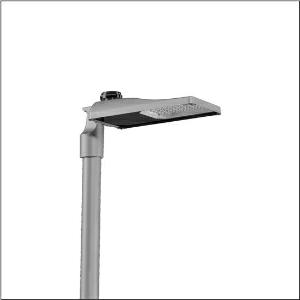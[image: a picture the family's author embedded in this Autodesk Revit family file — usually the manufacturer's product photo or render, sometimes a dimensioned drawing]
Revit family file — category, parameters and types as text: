
# Revit family: streetlight_sl_31_mini___st1_0a_5xh6d35n08ha_c5a6
name_source: partatom
category: Lighting Fixtures
units: mm (PartAtom-declared; Revit-internal decimal feet)

## family parameters
Cut with Voids When Loaded = No
Host = Face
Light Source = No
Part Type = Normal
Room Calculation Point = No
Round Connector Dimension = Use Diameter
Shared = No

## types (1)
- --- (1 x LED, 9240 lm, 68.3 W, 3000K)
    Apparent Load = 68 VA
    CIE Flux Codes = 37 72 97 100 100
    Color Rendering = 70
    Color Temperature = 3000K
    Default Elevation = 1800 mm
    Description = Streetlight SL 31 mini, mast luminaire, primary light control with lens, of PMMA, primary optical cover: cover, of toughened safety glass, transparent, light distribution: ST1.0a, light emission: direct distribution, primary light characteristic: asymmetric, installation type: post-top, side-entry, LED, High Power LED, rated luminous flux: 9.240lm, luminous efficacy: 135lm/W, light colour: 730, colour temperature: 3000K, control: presetting dimming linear, flexible luminous flux parameterisation, time-dependent luminous flux control, constant luminous flux control, intelligent temperature release in ECG and LED module, overheat protection, with cable H07RN-F 3x 1.5mm², mains connection: 220..240V, AC, 50/60Hz, connection cable pre-assembled, cable length: 8,5m, start of lifetime: 68W, end of service life: 75W, reduction: 30W, luminaire housing, of diecast aluminium, powder-coated, Siteco® metallic grey (DB 702S), corrosivity category C5 high according to DIN EN ISO 12944, no sealing on luminaire upper side, inclination: -15°..+20° (post-top) | -20°..+20° (side-entry), adjustable in 5° steps, mast flange (76/60mm) included as standard, multi-level sealing system, sealing non-destructively replaceable, protection rating (complete): IP66, insulation class (complete): insulation class I (protective earthing), certification: CE, ENEC, ENEC+, VDE, UKCA, impact resistance: IK09, permissible operating ambient temperature for outdoor applications: -40..+50°C, standard-compliant lighting for roads and squares, packaging unit: 1 piece

Light Distribution: ST1.0a
    Height = 76 mm
    Lamp = 1 x LED
    Lamp Light Flux = 9240 lm
    Lamp Power = 68.3 W
    Lamp count = 1
    Length = 547 mm
    Luminous efficacy = 135 lm/W
    Manufacturer = Siteco
    ModVariant = No
    Model = 5XH6D35N08HA
    Number of Poles = 1
    OnlyDefault = Yes
    Power Factor = 1
    Product Name = Streetlight SL 31 mini | ST1.0a
    Product group = mast luminaire | pylon top
    ProductGroupID = 6100
    Protection Class = Protection class I
    Protection Degree = IP 66
    RLX_Detail_Level = 1
    RLX_Emergency_Light_Flux = 0 lm
    RLX_Emergency_Type = 0
    RLX_Emergency_Type_DB = No
    RlxData = <blob elided: 40277 chars, md5=e69efe5d>
    Socket = socket
    Standby Power = 0 W
    System Light Flux = 9240 lm
    System Power = 68 W
    Type Comments = factory setting: luminous flux: 100 % | dim-lin: 254 | 693 mA
    Type Image = l_1300322.jpg
    URL = http://relux.com
    VarID = @adj_011481
    Voltage = 0 V
    Weight = 0.00 kg
    Width = 265 mm

## geometry (parser evidence)
native form markers: Blend x4, Sweep x10
no freeform markers — native parametric forms only
